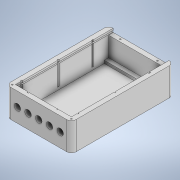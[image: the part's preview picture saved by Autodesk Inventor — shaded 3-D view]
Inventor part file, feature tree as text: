
AUTODESK INVENTOR PART (.ipt)
format: ipt  version: 2020 (Build 240168000, 168)  size: 566,272 bytes
history: native  units: mm
features: sketch x10, extrude x8, fillet x6, hole x3, plane x1
ambient origin geometry x8: Origin, YZ Plane, XZ Plane, XY Plane, X Axis, Y Axis, Z Axis, Center Point
bodies: Solid1 (feature_tree)
feature tree (28):
  sketch  "Sketch1"  dims[d0=60.0mm d1=100.0mm]
  extrude  "Extrusion1"  Depth=100.0mm
  extrude  "Extrusion2"  Depth=110.0mm
  fillet  "Fillet1"  Radius=30.0mm
  extrude  "Extrusion3"  Depth=5.0mm
  plane  "Work Plane1"
  extrude  "Extrusion4"  Depth=10.0mm TaperAngle=0.0deg
  extrude  "Extrusion5"  Depth=2.0mm
  hole  "Hole1"  [1 undecoded]
  hole  "Hole3"  [1 undecoded]
  hole  "Hole4"  [1 undecoded]
  extrude  "Extrusion6"  Depth=3.0mm
  fillet  "Fillet2"  Radius=7.0mm
  fillet  "Fillet3"  Radius=2.5mm
  extrude  "Extrusion7"  TaperAngle=45.0deg  [1 undecoded]
  fillet  "Fillet4"  Radius=2.5mm
  fillet  "Fillet5"  [1 undecoded]
  extrude  "Extrusion8"  Depth=20.0mm
  fillet  "Fillet6"  [1 undecoded]
  sketch  "Sketch2"  dims[d2=70.0mm d3=110.0mm d4=30.0mm d5=0.0mm]
  sketch  "Sketch3"  dims[d6=5.0mm d7=0.0mm d8=5.0mm]
  sketch  "Sketch4"  dims[d9=4.0mm d10=10.0mm d11=0.0mm]
  sketch  "Sketch5"  dims[d12=0.25mm d17=2.0mm]
  sketch  "Sketch7"  dims[d19=1.5mm d20=63.0mm]
  sketch  "Sketch8"  dims[d21=1.5mm d22=105.0mm d23=0.0mm]
  sketch  "Sketch9"  dims[d24=41.0mm d25=73.0mm]
  sketch  "Sketch10"  dims[d26=3.0mm d27=0.0mm d28=7.0mm d29=7.0mm]
  sketch  "Sketch11"  dims[d30=50.0mm d32=11.5mm d33=10.0mm d35=10.0mm d37=7.0mm d38=6.0mm d39=3.023mm d40=2.0mm d41=14.3117mm d42=8.0mm d43=20.594885mm d55=2.5mm d56=45.0deg d57=2.5mm d58=135.0deg d59=1.5mm d60=6.0mm d61=2.5mm d62=1.0mm d63=14.3117mm d64=40.0mm d65=20.594885mm d66=20.0mm d67=180.0deg d68=20.0mm d69=1.5mm d70=6.0mm d71=2.5mm d72=1.0mm d73=14.3117mm d74=40.0mm d75=20.594885mm d76=1.0mm d77=100.0mm d78=62.0mm d79=2.0mm d80=25.0mm d81=0.0mm d82=1.0mm d83=1.0mm d84=62.0mm d85=2.0mm d86=62.0mm d87=2.0mm d88=35.0mm d90=45.0mm d91=43.27457mm d92=25.0mm d93=0.0mm d94=1.0mm d95=1.0mm d96=1.0mm d97=2.0mm d98=2.0mm d100=13.0mm d101=13.0mm d102=2.0mm d103=1.0mm d104=25.0mm d105=0.0mm d106=1.0mm]
note: 6 required parameter values undecoded (feature->parameter linkage not recoverable at this tier; creation-order binding heuristic only, values carry confidence <= 0.55)
